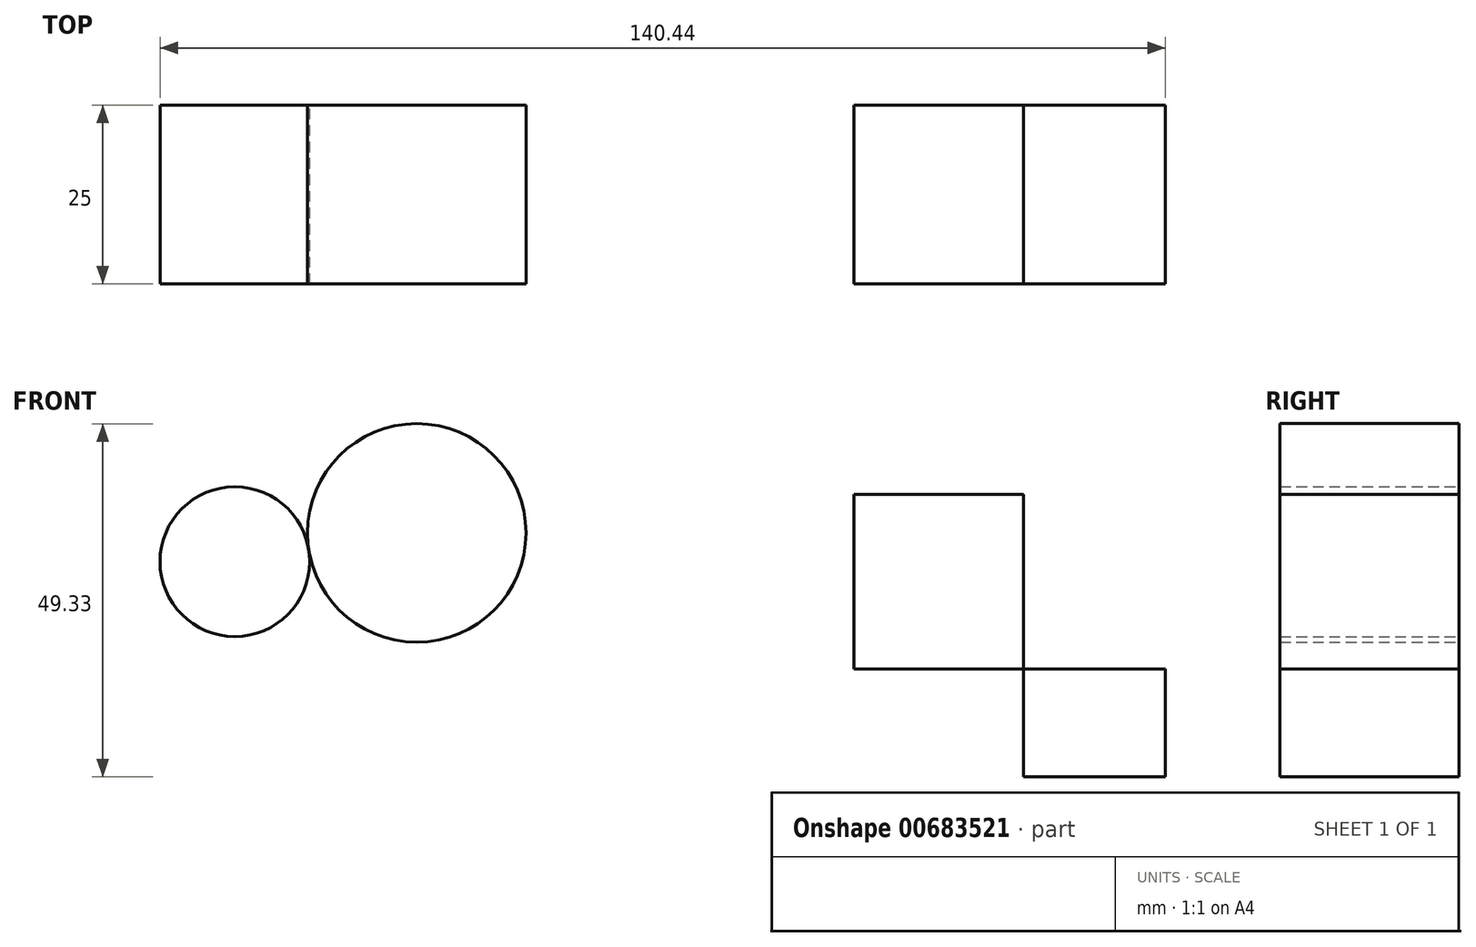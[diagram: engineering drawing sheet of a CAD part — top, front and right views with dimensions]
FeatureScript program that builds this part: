
annotation { "Feature Type Name" : "Feature", "Feature Type Description" : "" }
export const myFeature = defineFeature(function(context is Context, id is Id, definition is map)
    precondition{}
    {
        {
            var Q0;
            Q0=qCreatedBy(makeId("Front.planeOp"),FACE);
            var sketch = newSketch(context, id + "F0", { "sketchPlane" : qUnion([Q0])});
            skCircle(sketch, "E0", {"center": v(-61.68, 34.42) * mm, "radius": 10.45 * mm});
            skCircle(sketch, "E1", {"center": v(-36.28, 38.43) * mm, "radius": 15.26 * mm});
            skLineSegment(sketch, "E2.bottom", {"start": v(24.82, 43.8) * mm, "end": v(48.45, 43.8) * mm});
            skLineSegment(sketch, "E2.top", {"start": v(24.82, 19.42) * mm, "end": v(48.45, 19.42) * mm});
            skLineSegment(sketch, "E2.left", {"start": v(24.82, 43.8) * mm, "end": v(24.82, 19.42) * mm});
            skLineSegment(sketch, "E2.right", {"start": v(48.45, 43.8) * mm, "end": v(48.45, 19.42) * mm});
            skLineSegment(sketch, "E3.bottom", {"start": v(48.45, 19.42) * mm, "end": v(68.3, 19.42) * mm});
            skLineSegment(sketch, "E3.top", {"start": v(48.45, 4.36) * mm, "end": v(68.3, 4.36) * mm});
            skLineSegment(sketch, "E3.left", {"start": v(48.45, 19.42) * mm, "end": v(48.45, 4.36) * mm});
            skLineSegment(sketch, "E3.right", {"start": v(68.3, 19.42) * mm, "end": v(68.3, 4.36) * mm});
            skSolve(sketch);
        }
        {
            var Q0;
            Q0 = qSketchRegion(id + "F0", true);
            extrude(context, id + "F1", {"entities" : qUnion([Q0]), "depth" : 25 * mm, "offsetDistance" : 25 * mm});
        }
    });
